# Revit family: 3100.117.4-118.4 Down Pipe Junction 80x80 SE
name_source: partatom
category: Plumbing Fixtures
units: mm (PartAtom-declared; Revit-internal decimal feet)

## family parameters
Always vertical = Yes
Cut with Voids When Loaded = No
OmniClass Number = 23.45.00.00
OmniClass Title = Sanitary, Laundry, and Cleaning Equipment
Part Type = Normal
Room Calculation Point = No
Round Connector Dimension = Use Diameter
Shared = No
Work Plane-Based = No

## types (2) — shared parameters
CW Connection = No
HW Connection = No
Manufacturer = Aquanight Industries Ltd
Overflow = No
URL = www.aquaknight.co.nz
Vent Connection = Yes
Waste Connection = Yes
zero-valued in all types: Default Elevation

## per-type parameters (varying)
| type | Description | Model | Non-Vented | Vented |
| 3100.118.4 80x80 Non-Vented | Down-Pipe Junction 80mm Inlet w 80mm Outlet Non-Vented Side Exit Small Flange | 3100.118.4 | Yes | No |
| 3100.117.4 80x80 Vented | Down-Pipe Junction 80mm Inlet w 80mm Outlet Vented Side Exit Small Flange | 3100.117.4 | No | Yes |

## geometry (parser evidence)
native form markers: Sweep x2
no freeform markers — native parametric forms only
